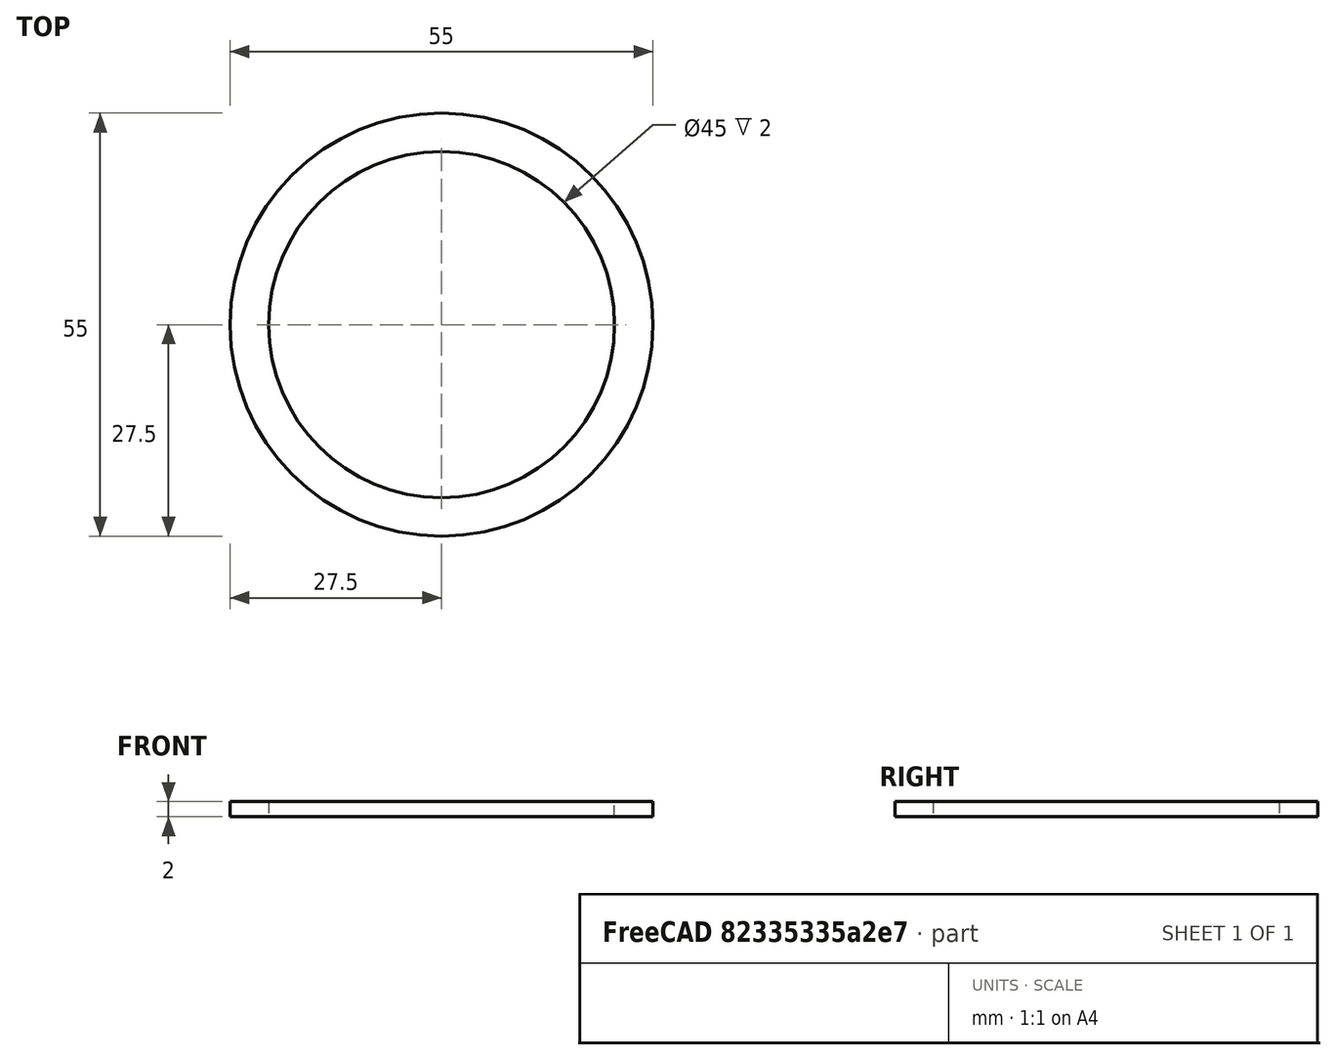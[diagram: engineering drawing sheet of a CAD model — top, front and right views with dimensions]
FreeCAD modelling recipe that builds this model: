
FCSTD DOCUMENT  (FreeCAD 0.21R33771 (Git))
Label: washer-air-gasket
License: All rights reserved
LicenseURL: http://en.wikipedia.org/wiki/All_rights_reserved
objects: Sketcher::SketchObject×1, PartDesign::Pad×1, PartDesign::Body×1
note: 4 computed .brp shape members not serialized (recipe doc carries the construction recipe); baked Part::Feature solids carry a one-line shape summary decoded from their .brp

FEATURE [Sketcher::SketchObject] Sketch
  FullyConstrained = true
  MapMode = 5
  Support = -> [XY_Plane]
  sketch-geometry (2):
    g0: Circle CenterX=0 CenterY=0 CenterZ=0 NormalX=0 NormalY=0 NormalZ=1 AngleXU=0 Radius=22.5
    g1: Circle CenterX=0 CenterY=0 CenterZ=0 NormalX=0 NormalY=0 NormalZ=1 AngleXU=0 Radius=27.5
  constraints (4):
    c: Coincident(g0,g-1)
    c: Coincident(g1,g0)
    c: Diameter(g0) = 45
    c: Diameter(g1) = 55
FEATURE [PartDesign::Pad] Pad
  Direction = (0,0,1)
  Length = 2
  Length2 = 10
  Profile = -> Sketch
  ReferenceAxis = -> Sketch [N_Axis]
  Type = 0
FEATURE [PartDesign::Body] Body
  Group = -> [Sketch,Pad]
  Origin = -> Origin
  Tip = -> Pad
